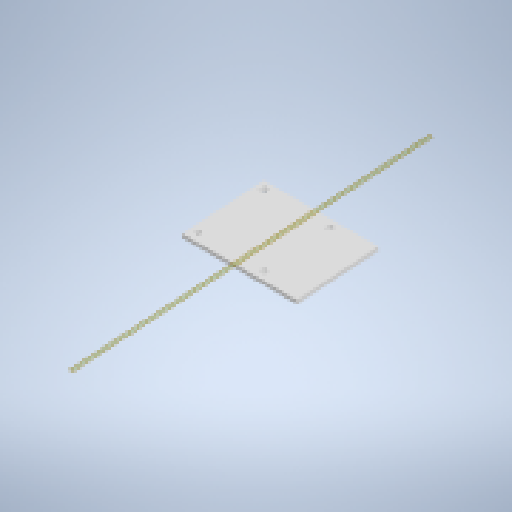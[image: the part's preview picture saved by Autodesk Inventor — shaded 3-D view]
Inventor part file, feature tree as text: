
AUTODESK INVENTOR PART (.ipt)
format: ipt  version: 2023.2 (Build 272271000, 271)  size: 166,400 bytes
history: native  units: mm
features: other x3, hole x2, plane x1, sketch x1, extrude x1
ambient origin geometry x8: Origin, YZ Plane, XZ Plane, XY Plane, X Axis, Y Axis, Z Axis, Center Point
bodies: Body1 (feature_tree)
feature tree (8):
  plane  "Work Plane1"
  sketch  "Sketch2"  dims[d15=125.2mm d16=125.2mm d23=50.0mm d28=6.0mm d29=0.0mm d30=12.3mm d31=100.6mm d32=12.3mm d33=100.6mm d34=5.1mm d35=6.0mm d36=9.2mm d37=2.0mm d38=90.0deg d39=8.0mm d40=20.594885mm d41=7.2mm d42=6.0mm d43=12.25mm d44=2.0mm d45=90.0deg d46=8.0mm d47=20.594885mm]
  extrude  "Extrusion2"  Depth=6.0mm TaperAngle=0.0deg
  hole  "Hole1"  [1 undecoded]
  hole  "Hole2"  [1 undecoded]
  parser-record x1  (decoder bookkeeping rows leaked as tree rows — omitted from the tree; the rows remain in map.json)
  other  "Main Assembly.iam"
  other  "C beam extrusion 500:1"
note: 2 required parameter values undecoded (feature->parameter linkage not recoverable at this tier; creation-order binding heuristic only, values carry confidence <= 0.55)
note: 1 file-system path scrubbed to <path> (originals preserved in map.json)
